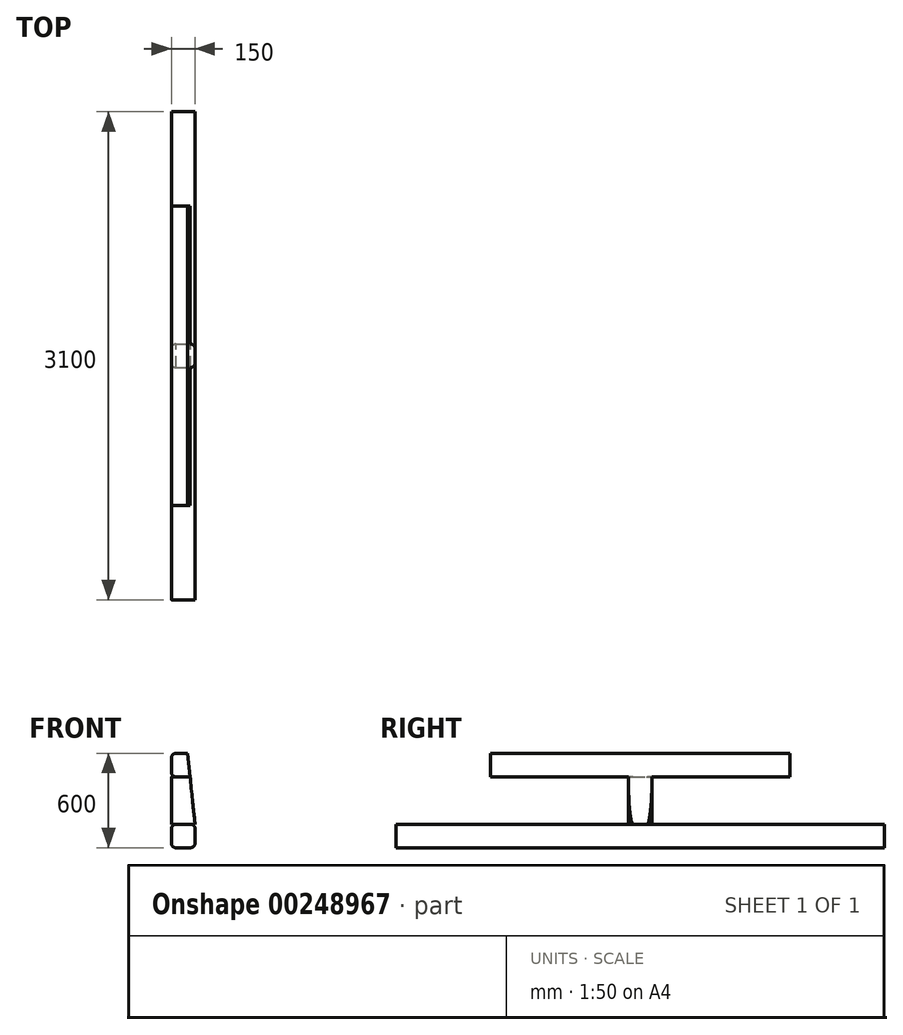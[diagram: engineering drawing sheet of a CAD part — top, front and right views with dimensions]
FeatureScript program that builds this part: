
annotation { "Feature Type Name" : "Feature", "Feature Type Description" : "" }
export const myFeature = defineFeature(function(context is Context, id is Id, definition is map)
    precondition{}
    {
        {
            var Q0;
            Q0=qCreatedBy(makeId("Front.planeOp"),FACE);
            var sketch = newSketch(context, id + "F0", { "sketchPlane" : qUnion([Q0])});
            skLineSegment(sketch, "E0.bottom", {"start": v(45, 75) * mm, "end": v(-45, 75) * mm});
            skLineSegment(sketch, "E0.top", {"start": v(45, -75) * mm, "end": v(-45, -75) * mm});
            skLineSegment(sketch, "E0.left", {"start": v(75, 45) * mm, "end": v(75, -45) * mm});
            skLineSegment(sketch, "E0.right", {"start": v(-75, 45) * mm, "end": v(-75, -45) * mm});
            skPoint(sketch, "E0.middle", {"position": v(0, 0) * mm});
            skPoint(sketch, "E1.visualSharp", {"position": v(75, 75) * mm});
            skArc(sketch, "E1.filletArc", {"start": v(75, 45) * mm, "mid": v(66.21, 66.21) * mm, "end": v(45, 75) * mm});
            skPoint(sketch, "E2.visualSharp", {"position": v(75, -75) * mm});
            skArc(sketch, "E2.filletArc", {"start": v(45, -75) * mm, "mid": v(66.21, -66.21) * mm, "end": v(75, -45) * mm});
            skPoint(sketch, "E3.visualSharp", {"position": v(-75, -75) * mm});
            skArc(sketch, "E3.filletArc", {"start": v(-75, -45) * mm, "mid": v(-66.21, -66.21) * mm, "end": v(-45, -75) * mm});
            skPoint(sketch, "E4.visualSharp", {"position": v(-75, 75) * mm});
            skArc(sketch, "E4.filletArc", {"start": v(-45, 75) * mm, "mid": v(-66.21, 66.21) * mm, "end": v(-75, 45) * mm});
            skSolve(sketch);
        }
        {
            var Q0;
            Q0 = qSketchRegion(id + "F0", true);
            extrude(context, id + "F1", {"entities" : qUnion([Q0]), "depth" : 3100 * mm});
        }
        {
            var Q0;
            Q0=makeQuery(id+"F1.opExtrude","CAP_FACE",FACE,{"disambiguationData":[OSD([sQuery(id+"F0.wireOp",EDGE,"E0.bottom"),sQuery(id+"F0.wireOp",EDGE,"E0.top"),sQuery(id+"F0.wireOp",EDGE,"E0.left"),sQuery(id+"F0.wireOp",EDGE,"E0.right"),sQuery(id+"F0.wireOp",EDGE,"E1.filletArc"),sQuery(id+"F0.wireOp",EDGE,"E2.filletArc"),sQuery(id+"F0.wireOp",EDGE,"E3.filletArc"),sQuery(id+"F0.wireOp",EDGE,"E4.filletArc")])],"isStart":true});
            var sketch = newSketch(context, id + "F2", { "sketchPlane" : qUnion([Q0])});
            skLineSegment(sketch, "E5.bottom", {"start": v(45, 525) * mm, "end": v(-45, 525) * mm});
            skLineSegment(sketch, "E5.top", {"start": v(45, 375) * mm, "end": v(-45, 375) * mm});
            skLineSegment(sketch, "E5.left", {"start": v(75, 495) * mm, "end": v(75, 405) * mm});
            skLineSegment(sketch, "E5.right", {"start": v(-75, 495) * mm, "end": v(-75, 405) * mm});
            skPoint(sketch, "E5.middle", {"position": v(0, 450) * mm});
            skPoint(sketch, "E6.visualSharp", {"position": v(-75, 375) * mm});
            skArc(sketch, "E6.filletArc", {"start": v(-75, 405) * mm, "mid": v(-66.21, 383.79) * mm, "end": v(-45, 375) * mm});
            skPoint(sketch, "E7.visualSharp", {"position": v(75, 375) * mm});
            skArc(sketch, "E7.filletArc", {"start": v(45, 375) * mm, "mid": v(66.21, 383.79) * mm, "end": v(75, 405) * mm});
            skPoint(sketch, "E8.visualSharp", {"position": v(-75, 525) * mm});
            skArc(sketch, "E8.filletArc", {"start": v(-45, 525) * mm, "mid": v(-66.21, 516.21) * mm, "end": v(-75, 495) * mm});
            skPoint(sketch, "E9.visualSharp", {"position": v(75, 525) * mm});
            skArc(sketch, "E9.filletArc", {"start": v(75, 495) * mm, "mid": v(66.21, 516.21) * mm, "end": v(45, 525) * mm});
            skSolve(sketch);
        }
        {
            var Q0;
            Q0 = qSketchRegion(id + "F2", true);
            extrude(context, id + "F3", {"entities" : qUnion([Q0]), "operationType" : NewBodyOperationType.ADD, "oppositeDirection" : true, "depth" : 2500 * mm, "hasSecondDirection" : true, "secondDirectionOppositeDirection" : true, "secondDirectionDepth" : 600 * mm});
        }
        {
            var Q0;
            Q0=makeQuery(id+"F1.opExtrude","SWEPT_FACE",FACE,{"disambiguationData":[OSD([sQuery(id+"F0.wireOp",EDGE,"E0.bottom")])]});
            var sketch = newSketch(context, id + "F4", { "sketchPlane" : qUnion([Q0])});
            skLineSegment(sketch, "E10.bottom", {"start": v(-45, -1625) * mm, "end": v(45, -1625) * mm});
            skLineSegment(sketch, "E10.top", {"start": v(-45, -1475) * mm, "end": v(45, -1475) * mm});
            skLineSegment(sketch, "E10.left", {"start": v(-75, -1595) * mm, "end": v(-75, -1505) * mm});
            skLineSegment(sketch, "E10.right", {"start": v(75, -1595) * mm, "end": v(75, -1505) * mm});
            skPoint(sketch, "E10.middle", {"position": v(0, -1550) * mm});
            skPoint(sketch, "E11.visualSharp", {"position": v(75, -1625) * mm});
            skArc(sketch, "E11.filletArc", {"start": v(45, -1625) * mm, "mid": v(66.21, -1616.21) * mm, "end": v(75, -1595) * mm});
            skPoint(sketch, "E12.visualSharp", {"position": v(75, -1475) * mm});
            skArc(sketch, "E12.filletArc", {"start": v(75, -1505) * mm, "mid": v(66.21, -1483.79) * mm, "end": v(45, -1475) * mm});
            skPoint(sketch, "E13.visualSharp", {"position": v(-75, -1475) * mm});
            skArc(sketch, "E13.filletArc", {"start": v(-45, -1475) * mm, "mid": v(-66.21, -1483.79) * mm, "end": v(-75, -1505) * mm});
            skPoint(sketch, "E14.visualSharp", {"position": v(-75, -1625) * mm});
            skArc(sketch, "E14.filletArc", {"start": v(-75, -1595) * mm, "mid": v(-66.21, -1616.21) * mm, "end": v(-45, -1625) * mm});
            skSolve(sketch);
        }
        {
            var Q0;
            Q0 = qSketchRegion(id + "F4", true);
            var Q1;
            Q1=makeQuery(id+"F3.opExtrude","SWEPT_FACE",FACE,{"disambiguationData":[OSD([sQuery(id+"F2.wireOp",EDGE,"E5.top")])]});
            extrude(context, id + "F5", {"entities" : qUnion([Q0]), "operationType" : NewBodyOperationType.ADD, "endBound" : BoundingType.UP_TO_SURFACE, "endBoundEntityFace" : qUnion([Q1]), "depth" : 25 * mm});
        }
        {
            var Q0;
            Q0=makeQuery(id+"F1.opExtrude","CAP_FACE",FACE,{"disambiguationData":[OSD([sQuery(id+"F0.wireOp",EDGE,"E0.bottom"),sQuery(id+"F0.wireOp",EDGE,"E0.top"),sQuery(id+"F0.wireOp",EDGE,"E0.left"),sQuery(id+"F0.wireOp",EDGE,"E0.right"),sQuery(id+"F0.wireOp",EDGE,"E1.filletArc"),sQuery(id+"F0.wireOp",EDGE,"E2.filletArc"),sQuery(id+"F0.wireOp",EDGE,"E3.filletArc"),sQuery(id+"F0.wireOp",EDGE,"E4.filletArc")])],"isStart":true});
            var sketch = newSketch(context, id + "F6", { "sketchPlane" : qUnion([Q0])});
            skLineSegment(sketch, "E15", {"start": v(-27.7, 525) * mm, "end": v(-75, 75) * mm});
            skPoint(sketch, "E15.endSnap0", {"position": v(-66.21, 75) * mm});
            skLineSegment(sketch, "E16", {"start": v(-75, 75) * mm, "end": v(-204.01, 75) * mm});
            skLineSegment(sketch, "E17", {"start": v(-204.01, 75) * mm, "end": v(-204.01, 525) * mm});
            skLineSegment(sketch, "E18", {"start": v(-204.01, 525) * mm, "end": v(-27.7, 525) * mm});
            skSolve(sketch);
        }
        {
            var Q0;
            Q0 = qSketchRegion(id + "F6", true);
            extrude(context, id + "F7", {"entities" : qUnion([Q0]), "operationType" : NewBodyOperationType.REMOVE, "oppositeDirection" : true, "depth" : 3500 * mm});
        }
    });
